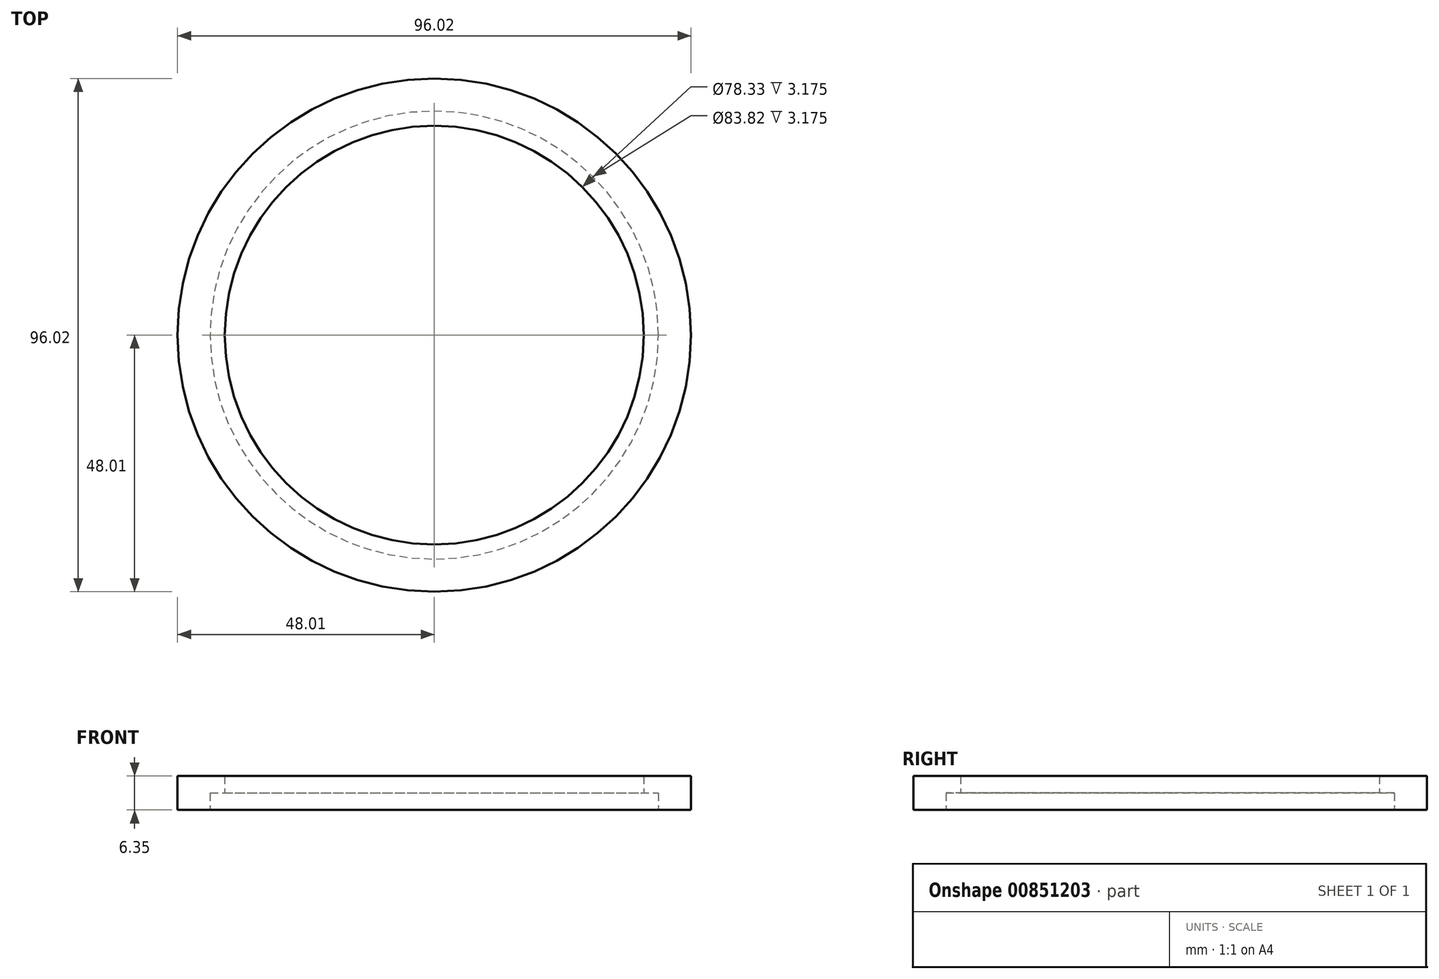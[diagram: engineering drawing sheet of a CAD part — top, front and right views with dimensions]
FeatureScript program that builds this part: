
annotation { "Feature Type Name" : "Feature", "Feature Type Description" : "" }
export const myFeature = defineFeature(function(context is Context, id is Id, definition is map)
    precondition{}
    {
        {
            var Q0;
            Q0=qCreatedBy(makeId("Top.planeOp"),FACE);
            var sketch = newSketch(context, id + "F0", { "sketchPlane" : qUnion([Q0])});
            skCircle(sketch, "E0", {"center": v(0, 0) * mm, "radius": 48 * mm});
            skCircle(sketch, "E1", {"center": v(0, 0) * mm, "radius": 39.17 * mm});
            skSolve(sketch);
        }
        {
            var Q0;
            Q0=qSketchRegion(id+"F0",true);
            extrude(context, id + "F1", {"entities" : qUnion([Q0]), "depth" : 6.35 * mm, "offsetDistance" : 25.4 * mm});
        }
        {
            var Q0;
            Q0=makeQuery(id+"F1.opExtrude","CAP_FACE",FACE,{"disambiguationData":[OSD([sQuery(id+"F0.wireOp",EDGE,"E0"),sQuery(id+"F0.wireOp",EDGE,"E1")])],"isStart":true});
            var sketch = newSketch(context, id + "F2", { "sketchPlane" : qUnion([Q0])});
            skCircle(sketch, "E2", {"center": v(0, 0) * mm, "radius": 41.91 * mm});
            skSolve(sketch);
        }
        {
            var Q0;
            Q0 = qSketchRegion(id + "F2", true);
            extrude(context, id + "F3", {"entities" : qUnion([Q0]), "operationType" : NewBodyOperationType.REMOVE, "oppositeDirection" : true, "depth" : 3.17 * mm, "offsetDistance" : 25.4 * mm});
        }
    });
